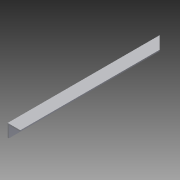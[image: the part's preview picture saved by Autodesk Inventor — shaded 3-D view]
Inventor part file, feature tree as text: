
AUTODESK INVENTOR PART (.ipt)
format: ipt  version: 2014 (Build 180170000, 170)  size: 81,408 bytes
history: native  units: in
note: dims shown in document units (in); Inventor stores cm internally (conversion verified against a paired STEP export)
features: extrude x2, sketch x2
ambient origin geometry x8: Origin, YZ Plane, XZ Plane, XY Plane, X Axis, Y Axis, Z Axis, Center Point
bodies: Solid1 (feature_tree)
feature tree (4):
  extrude  "Extrusion1"  Depth=0.5in
  extrude  "Extrusion2"  Depth=0.45in
  sketch  "Sketch1"  dims[d0=0.5in d1=0.5in]
  sketch  "Sketch2"  dims[d2=0.05in d3=0.45in d4=6.0in d5=0.0in d6=45.0deg d8=9.0in d9=0.0in]
